# Revit family: Radian NEW 12
name_source: partatom
category: Осветительные приборы
revit_build: Autodesk Revit 2017 (Build: 20160225_1515(x64)
units: mm (PartAtom-declared; Revit-internal decimal feet)

## family parameters
Всегда вертикально = Да
Заголовок OmniClass = Luminaries for Internal Lighting
Источник света = Да
Номер OmniClass = 23.80.70.11
Общий = Нет
Основа = Потолок
При загрузке вырезать с полостями = Нет
Размер круглого соединителя = Использовать диаметр
Тип детали = Нормальный
Точка расчета площади = Нет

## types (2) — shared parameters
Видимая форма излучения при визуализации = Да
Изготовитель = LEDEL
Излучение по диаметру окружности = 68.5 мм
Комментарии к типоразмеру = Бытовые
Полная установленная мощность = 5 В·А
Светофильтр = 16777215
Смещение цветовой температуры при затухании лампы = <Нет>
Угол наклона = 90.00°

## per-type parameters (varying)
| type | Артикул | Файл фотометрической сетки |
| Radian NEW 12 3.0К | 203100500833400 | Radian NEW 12-5-D-3.0K-03.ies |
| Radian NEW 12 5.0К | 503001 | Radian NEW 12-5-D-5.0K-03.ies |

## geometry (parser evidence)
native form markers: Sweep x2
no freeform markers — native parametric forms only
